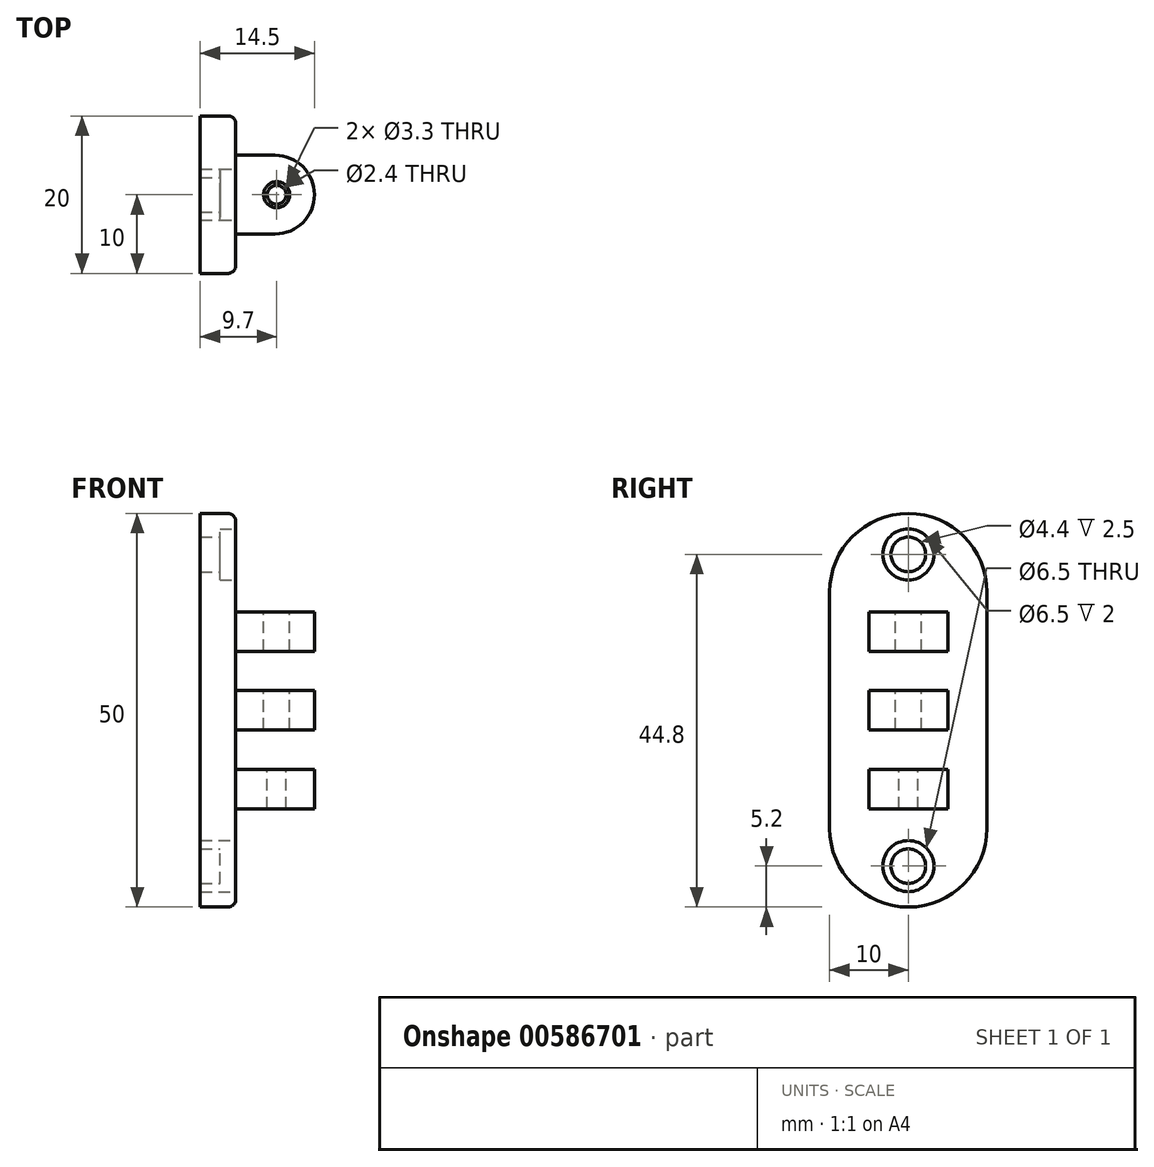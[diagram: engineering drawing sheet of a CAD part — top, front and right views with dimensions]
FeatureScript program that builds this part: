
annotation { "Feature Type Name" : "Feature", "Feature Type Description" : "" }
export const myFeature = defineFeature(function(context is Context, id is Id, definition is map)
    precondition{}
    {
        {
            var Q0;
            Q0=qCreatedBy(makeId("Right.planeOp"),FACE);
            var sketch = newSketch(context, id + "F0", { "sketchPlane" : qUnion([Q0])});
            skLineSegment(sketch, "E0.bottom", {"start": v(0, 25) * mm, "end": v(0, 25) * mm});
            skLineSegment(sketch, "E0.top", {"start": v(0, -25) * mm, "end": v(0, -25) * mm});
            skLineSegment(sketch, "E0.left", {"start": v(-10, 15) * mm, "end": v(-10, -15) * mm});
            skLineSegment(sketch, "E0.right", {"start": v(10, 15) * mm, "end": v(10, -15) * mm});
            skPoint(sketch, "E0.middle", {"position": v(0, 0) * mm});
            skPoint(sketch, "E1.visualSharp", {"position": v(-10, 25) * mm});
            skArc(sketch, "E1.filletArc", {"start": v(0, 25) * mm, "mid": v(-7.07, 22.07) * mm, "end": v(-10, 15) * mm});
            skPoint(sketch, "E2.visualSharp", {"position": v(10, 25) * mm});
            skArc(sketch, "E2.filletArc", {"start": v(10, 15) * mm, "mid": v(7.07, 22.07) * mm, "end": v(0, 25) * mm});
            skPoint(sketch, "E3.visualSharp", {"position": v(10, -25) * mm});
            skArc(sketch, "E3.filletArc", {"start": v(0, -25) * mm, "mid": v(7.07, -22.07) * mm, "end": v(10, -15) * mm});
            skPoint(sketch, "E4.visualSharp", {"position": v(-10, -25) * mm});
            skArc(sketch, "E4.filletArc", {"start": v(-10, -15) * mm, "mid": v(-7.07, -22.07) * mm, "end": v(0, -25) * mm});
            skCircle(sketch, "E5", {"center": v(0, 19.8) * mm, "radius": 2.2 * mm});
            skCircle(sketch, "E6.MirrorC", {"center": v(0, -19.8) * mm, "radius": 2.2 * mm});
            skLineSegment(sketch, "E7.bottom", {"start": v(-5, 12.5) * mm, "end": v(5, 12.5) * mm});
            skLineSegment(sketch, "E7.top", {"start": v(-5, 7.5) * mm, "end": v(5, 7.5) * mm});
            skLineSegment(sketch, "E7.left", {"start": v(-5, 12.5) * mm, "end": v(-5, 7.5) * mm});
            skLineSegment(sketch, "E7.right", {"start": v(5, 12.5) * mm, "end": v(5, 7.5) * mm});
            skPoint(sketch, "E7.middle", {"position": v(0, 10) * mm});
            skLineSegment(sketch, "E8.0.1.0", {"start": v(-5, 2.5) * mm, "end": v(5, 2.5) * mm});
            skLineSegment(sketch, "E8.0.1.2", {"start": v(-5, -2.5) * mm, "end": v(5, -2.5) * mm});
            skLineSegment(sketch, "E8.0.1.3", {"start": v(5, 2.5) * mm, "end": v(5, -2.5) * mm});
            skLineSegment(sketch, "E8.0.1.4", {"start": v(-5, 2.5) * mm, "end": v(-5, -2.5) * mm});
            skLineSegment(sketch, "E8.0.2.0", {"start": v(-5, -7.5) * mm, "end": v(5, -7.5) * mm});
            skPoint(sketch, "E8.0.2.1", {"position": v(0, -10) * mm});
            skLineSegment(sketch, "E8.0.2.2", {"start": v(-5, -12.5) * mm, "end": v(5, -12.5) * mm});
            skLineSegment(sketch, "E8.0.2.3", {"start": v(5, -7.5) * mm, "end": v(5, -12.5) * mm});
            skLineSegment(sketch, "E8.0.2.4", {"start": v(-5, -7.5) * mm, "end": v(-5, -12.5) * mm});
            skLineSegment(sketch, "E8.direction1", {"start": v(-5, 12.5) * mm, "end": v(20, 12.5) * mm, "construction": true});
            skLineSegment(sketch, "E8.direction2", {"start": v(-5, 12.5) * mm, "end": v(-5, 2.5) * mm, "construction": true});
            skCircle(sketch, "E9", {"center": v(0, 19.8) * mm, "radius": 3.25 * mm});
            skCircle(sketch, "E10.MirrorC", {"center": v(0, -19.8) * mm, "radius": 3.25 * mm});
            skSolve(sketch);
        }
        {
            var Q0;
            Q0=qCreatedBy(makeId("Top.planeOp"),FACE);
            var sketch = newSketch(context, id + "F1", { "sketchPlane" : qUnion([Q0])});
            skLineSegment(sketch, "E11.bottom", {"start": v(0, 5) * mm, "end": v(5, 5) * mm});
            skLineSegment(sketch, "E11.top", {"start": v(0, -5) * mm, "end": v(5, -5) * mm});
            skLineSegment(sketch, "E11.left", {"start": v(0, 5) * mm, "end": v(0, -5) * mm});
            skLineSegment(sketch, "E11.right", {"start": v(10, 0) * mm, "end": v(10, 0) * mm});
            skPoint(sketch, "E12.visualSharp", {"position": v(10, 5) * mm});
            skArc(sketch, "E12.filletArc", {"start": v(10, 0) * mm, "mid": v(8.54, 3.54) * mm, "end": v(5, 5) * mm});
            skPoint(sketch, "E13.visualSharp", {"position": v(10, -5) * mm});
            skArc(sketch, "E13.filletArc", {"start": v(5, -5) * mm, "mid": v(8.54, -3.54) * mm, "end": v(10, 0) * mm});
            skCircle(sketch, "E14", {"center": v(5.2, 0) * mm, "radius": 1.65 * mm});
            skCircle(sketch, "E15", {"center": v(5.2, 0) * mm, "radius": 1.2 * mm});
            skLineSegment(sketch, "E16.bottom", {"start": v(0, 5) * mm, "end": v(0, 5) * mm});
            skLineSegment(sketch, "E16.top", {"start": v(0, -5) * mm, "end": v(0, -5) * mm});
            skLineSegment(sketch, "E17.bottom", {"start": v(0, 10) * mm, "end": v(-4.5, 10) * mm});
            skLineSegment(sketch, "E17.top", {"start": v(0, -10) * mm, "end": v(-4.5, -10) * mm});
            skLineSegment(sketch, "E17.left", {"start": v(0, 10) * mm, "end": v(0, -10) * mm});
            skLineSegment(sketch, "E17.right", {"start": v(-4.5, 10) * mm, "end": v(-4.5, -10) * mm});
            skSolve(sketch);
        }
        {
            var Q0;
            Q0=makeQuery(id+"F0.imprint","IMPRINT",FACE,{"disambiguationData":[TD([[makeQuery(id+"F0.imprint","IMPRINT",EDGE,{"derivedFrom":sQuery(id+"F0.wireOp",EDGE,"E0.left")}),1.0]])]});
            var Q1;
            Q1=makeQuery(id+"F0.imprint","IMPRINT",FACE,{"disambiguationData":[TD([[makeQuery(id+"F0.imprint","IMPRINT",EDGE,{"derivedFrom":sQuery(id+"F0.wireOp",EDGE,"E7.bottom")}),-1.0]])]});
            var Q2;
            Q2=makeQuery(id+"F0.imprint","IMPRINT",FACE,{"disambiguationData":[TD([[makeQuery(id+"F0.imprint","IMPRINT",EDGE,{"derivedFrom":sQuery(id+"F0.wireOp",EDGE,"E8.0.1.0")}),-1.0]])]});
            var Q3;
            Q3=makeQuery(id+"F0.imprint","IMPRINT",FACE,{"disambiguationData":[TD([[makeQuery(id+"F0.imprint","IMPRINT",EDGE,{"derivedFrom":sQuery(id+"F0.wireOp",EDGE,"E8.0.2.0")}),-1.0]])]});
            var Q4;
            Q4=makeQuery(id+"F0.imprint","IMPRINT",FACE,{"disambiguationData":[TD([[makeQuery(id+"F0.imprint","IMPRINT",EDGE,{"derivedFrom":sQuery(id+"F0.wireOp",EDGE,"E5")}),-1.0]])]});
            var Q5;
            Q5=makeQuery(id+"F0.imprint","IMPRINT",FACE,{"disambiguationData":[TD([[makeQuery(id+"F0.imprint","IMPRINT",EDGE,{"derivedFrom":sQuery(id+"F0.wireOp",EDGE,"E6.MirrorC")}),1.0]])]});
            extrude(context, id + "F2", {"entities" : qUnion([Q0, Q1, Q2, Q3, Q4, Q5]), "oppositeDirection" : true, "depth" : 4.5 * mm, "offsetDistance" : 25 * mm});
        }
        {
            var Q0;
            Q0=makeQuery(id+"F0.imprint","IMPRINT",FACE,{"disambiguationData":[TD([[makeQuery(id+"F0.imprint","IMPRINT",EDGE,{"derivedFrom":sQuery(id+"F0.wireOp",EDGE,"E7.bottom")}),-1.0]])]});
            var Q1;
            Q1=makeQuery(id+"F0.imprint","IMPRINT",FACE,{"disambiguationData":[TD([[makeQuery(id+"F0.imprint","IMPRINT",EDGE,{"derivedFrom":sQuery(id+"F0.wireOp",EDGE,"E8.0.1.0")}),-1.0]])]});
            var Q2;
            Q2=makeQuery(id+"F0.imprint","IMPRINT",FACE,{"disambiguationData":[TD([[makeQuery(id+"F0.imprint","IMPRINT",EDGE,{"derivedFrom":sQuery(id+"F0.wireOp",EDGE,"E8.0.2.0")}),-1.0]])]});
            extrude(context, id + "F3", {"entities" : qUnion([Q0, Q1, Q2]), "operationType" : NewBodyOperationType.ADD, "depth" : 10 * mm, "offsetDistance" : 25 * mm});
        }
        {
            var Q0;
            Q0=makeQuery(id+"F1.imprint","IMPRINT",FACE,{"disambiguationData":[TD([[makeQuery(id+"F1.imprint","IMPRINT",EDGE,{"derivedFrom":sQuery(id+"F1.wireOp",EDGE,"E11.bottom")}),-1.0]])]});
            var Q1;
            Q1=makeQuery(id+"F1.imprint","IMPRINT",FACE,{"disambiguationData":[TD([[makeQuery(id+"F1.imprint","IMPRINT",EDGE,{"derivedFrom":sQuery(id+"F1.wireOp",EDGE,"E15")}),1.0]])]});
            var Q2;
            Q2=makeQuery(id+"F1.imprint","IMPRINT",FACE,{"disambiguationData":[TD([[makeQuery(id+"F1.imprint","IMPRINT",EDGE,{"derivedFrom":sQuery(id+"F1.wireOp",EDGE,"E14")}),1.0]])]});
            var Q3;
            {var subQ3=sQuery(id+"F1.wireOp",EDGE,"E17.bottom");Q3=makeQuery(id+"F1.imprint","IMPRINT",FACE,{"disambiguationData":[TD([[makeQuery(id+"F1.imprint","IMPRINT",EDGE,{"derivedFrom":subQ3}),1.0]])]});}
            extrude(context, id + "F4", {"entities" : qUnion([Q0, Q1, Q2, Q3]), "operationType" : NewBodyOperationType.INTERSECT, "endBound" : BoundingType.SYMMETRIC, "depth" : 50 * mm, "offsetDistance" : 25 * mm});
        }
        {
            var Q0;
            Q0=makeQuery(id+"F1.imprint","IMPRINT",FACE,{"disambiguationData":[TD([[makeQuery(id+"F1.imprint","IMPRINT",EDGE,{"derivedFrom":sQuery(id+"F1.wireOp",EDGE,"E14")}),1.0]])]});
            var Q1;
            Q1=makeQuery(id+"F1.imprint","IMPRINT",FACE,{"disambiguationData":[TD([[makeQuery(id+"F1.imprint","IMPRINT",EDGE,{"derivedFrom":sQuery(id+"F1.wireOp",EDGE,"E15")}),1.0]])]});
            var Q2;
            Q2=makeQuery(id+"F3.opExtrude","SWEPT_FACE",FACE,{"disambiguationData":[OSD([sQuery(id+"F0.wireOp",EDGE,"E8.0.1.2")])]});
            var Q3;
            Q3=makeQuery(id+"F3.opExtrude","SWEPT_FACE",FACE,{"disambiguationData":[OSD([sQuery(id+"F0.wireOp",EDGE,"E7.bottom")])]});
            extrude(context, id + "F5", {"entities" : qUnion([Q0, Q1]), "operationType" : NewBodyOperationType.REMOVE, "endBound" : BoundingType.UP_TO_SURFACE, "oppositeDirection" : true, "depth" : 15.5 * mm, "endBoundEntityFace" : qUnion([Q2]), "offsetDistance" : 25 * mm, "hasSecondDirection" : true, "secondDirectionBound" : SecondDirectionBoundingType.UP_TO_SURFACE, "secondDirectionOppositeDirection" : false, "secondDirectionDepth" : 13.9 * mm, "secondDirectionBoundEntityFace" : qUnion([Q3])});
        }
        {
            var Q0;
            Q0=makeQuery(id+"F1.imprint","IMPRINT",FACE,{"disambiguationData":[TD([[makeQuery(id+"F1.imprint","IMPRINT",EDGE,{"derivedFrom":sQuery(id+"F1.wireOp",EDGE,"E15")}),1.0]])]});
            var Q1;
            Q1=sQuery(id+"F1.wireOp",EDGE,"E15");
            extrude(context, id + "F6", {"entities" : qUnion([Q0]), "operationType" : NewBodyOperationType.REMOVE, "surfaceEntities" : qUnion([Q1]), "oppositeDirection" : true, "depth" : 14.6 * mm, "offsetDistance" : 25 * mm, "hasSecondDirection" : true, "secondDirectionOppositeDirection" : true, "secondDirectionDepth" : 6.1 * mm});
        }
        {
            var Q0;
            Q0=makeQuery(id+"F0.imprint","IMPRINT",FACE,{"disambiguationData":[TD([[makeQuery(id+"F0.imprint","IMPRINT",EDGE,{"derivedFrom":sQuery(id+"F0.wireOp",EDGE,"E5")}),-1.0]])]});
            var Q1;
            Q1=makeQuery(id+"F0.imprint","IMPRINT",FACE,{"disambiguationData":[TD([[makeQuery(id+"F0.imprint","IMPRINT",EDGE,{"derivedFrom":sQuery(id+"F0.wireOp",EDGE,"E6.MirrorC")}),1.0]])]});
            extrude(context, id + "F7", {"entities" : qUnion([Q0, Q1]), "operationType" : NewBodyOperationType.REMOVE, "oppositeDirection" : true, "depth" : 2 * mm, "offsetDistance" : 25 * mm});
        }
        {
            var Q0;
            {var subQ0=sQuery(id+"F0.wireOp",EDGE,"E2.filletArc");var subQ1=sQuery(id+"F0.wireOp",EDGE,"E1.filletArc");var subQ2=sQuery(id+"F1.wireOp",EDGE,"E17.left");Q0=makeQuery(id+"F4.boolean.opBoolean","INTERSECT",EDGE,{"disambiguationData":[topologyDisambiguationEdgeConnected([makeQuery(id+"F2.opExtrude","SWEPT_FACE",FACE,{"disambiguationData":[OSD([subQ1,subQ0])]})])],"derivedFrom":[makeQuery(id+"F4.boolean.toolComplement.opBoolean","COPY",FACE,{"derivedFrom":makeQuery(id+"F4.opExtrude","SWEPT_FACE",FACE,{"disambiguationData":[OSD([subQ2]),TDD([makeQuery(id+"F1.imprint","IMPRINT",EDGE,{"disambiguationData":[TD([[makeQuery(id+"F1.imprint","INTERSECT",VERTEX,{"derivedFrom":[sQuery(id+"F1.wireOp",EDGE,"E11.bottom"),subQ2]}),1.0]])],"derivedFrom":subQ2})])]})}),makeQuery(id+"F4.boolean.toolComplement.opBoolean","COPY",FACE,{"derivedFrom":makeQuery(id+"F4.opExtrude","SWEPT_FACE",FACE,{"disambiguationData":[OSD([subQ2]),TDD([makeQuery(id+"F1.imprint","IMPRINT",EDGE,{"disambiguationData":[TD([[makeQuery(id+"F1.imprint","INTERSECT",VERTEX,{"derivedFrom":[sQuery(id+"F1.wireOp",EDGE,"E11.top"),subQ2]}),-1.0]])],"derivedFrom":subQ2})])]})})]});}
            var Q1;
            Q1=makeQuery(id+"F2.opExtrude","CAP_EDGE",EDGE,{"disambiguationData":[OSD([sQuery(id+"F0.wireOp",EDGE,"E0.left")])],"isStart":true});
            var Q2;
            {var subQ0=sQuery(id+"F0.wireOp",EDGE,"E4.filletArc");var subQ1=sQuery(id+"F0.wireOp",EDGE,"E3.filletArc");var subQ2=sQuery(id+"F1.wireOp",EDGE,"E17.left");Q2=makeQuery(id+"F4.boolean.opBoolean","INTERSECT",EDGE,{"disambiguationData":[topologyDisambiguationEdgeConnected([makeQuery(id+"F2.opExtrude","SWEPT_FACE",FACE,{"disambiguationData":[OSD([subQ1,subQ0])]})])],"derivedFrom":[makeQuery(id+"F4.boolean.toolComplement.opBoolean","COPY",FACE,{"derivedFrom":makeQuery(id+"F4.opExtrude","SWEPT_FACE",FACE,{"disambiguationData":[OSD([subQ2]),TDD([makeQuery(id+"F1.imprint","IMPRINT",EDGE,{"disambiguationData":[TD([[makeQuery(id+"F1.imprint","INTERSECT",VERTEX,{"derivedFrom":[sQuery(id+"F1.wireOp",EDGE,"E11.bottom"),subQ2]}),1.0]])],"derivedFrom":subQ2})])]})}),makeQuery(id+"F4.boolean.toolComplement.opBoolean","COPY",FACE,{"derivedFrom":makeQuery(id+"F4.opExtrude","SWEPT_FACE",FACE,{"disambiguationData":[OSD([subQ2]),TDD([makeQuery(id+"F1.imprint","IMPRINT",EDGE,{"disambiguationData":[TD([[makeQuery(id+"F1.imprint","INTERSECT",VERTEX,{"derivedFrom":[sQuery(id+"F1.wireOp",EDGE,"E11.top"),subQ2]}),-1.0]])],"derivedFrom":subQ2})])]})})]});}
            var Q3;
            Q3=makeQuery(id+"F2.opExtrude","CAP_EDGE",EDGE,{"disambiguationData":[OSD([sQuery(id+"F0.wireOp",EDGE,"E0.right")])],"isStart":true});
            fillet(context, id + "F8", {"entities" : qUnion([Q0, Q1, Q2, Q3]), "radius" : 1 * mm, "tangentPropagation" : true, "allowEdgeOverflow" : false});
        }
    });
